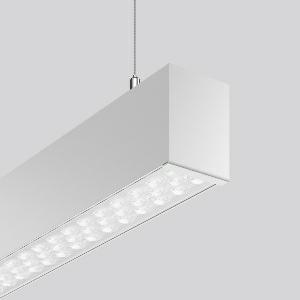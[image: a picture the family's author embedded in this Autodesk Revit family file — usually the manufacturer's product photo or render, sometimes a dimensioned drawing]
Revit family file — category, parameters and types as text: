
# Revit family: linedo_single_ip20_312563_000_1_f37b
name_source: partatom
category: Lighting Fixtures
units: mm (PartAtom-declared; Revit-internal decimal feet)

## family parameters
Cut with Voids When Loaded = No
Host = Face
Light Source = No
Part Type = Normal
Room Calculation Point = No
Round Connector Dimension = Use Diameter
Shared = No

## types (1)
- LINEDO single IP20 (1 x LED Modul 840, 4850 lm, 4000)
    Apparent Load = 31 VA
    CIE Flux Codes = 86 96 99 100 100
    Color Rendering = 80
    Color Temperature = 4000
    Default Elevation = 1800 mm
    Description = Series: LINEDO single IP20
Stylish pendant luminaire. Housing: extruded aluminium profile, anodised. End cap aluminium powder-coated, without visible screws. High-efficiency LED units with optimum light control thanks to clear plastic (PC) lens optics. 2-point steel cable suspension freely positionable and infinitely height-adjustable. With power cord (2.5 m). Please order canopy separately if required. Perfect for office areas (RUG < 19) and environments with computer screens in accordance with EN 12464-1. 
Colour: anodised aluminium
Length: 1700 mm
Width: 58 mm
Height: 76 mm
Suspension length: 100-1500 mm
Lamp: LED
Socket: without socket
Colour temperature: 4000K
Colour rendering index (CRI): 80
System power: 31 W
Rated luminous flux: 4850 lm
Beam angle Down: 59°
Luminous efficiency: 156 lm/W
Control gear: Regulated power supply
Protection class: I
Type of protection: IP 20
    Height = 76 mm
    Lamp = 1 x LED Modul 840
    Lamp Light Flux = 4850 lm
    Lamp count = 1
    Length = 1700 mm
    Lifetime = 50000 h
    Luminous efficacy = 156 lm/W
    Manufacturer = RZB
    ModVariant = No
    Model = 312563.000.1
    Mounting Place = Ceiling
    Mounting Type = Pendant
    Number of Poles = 1
    OnlyDefault = Yes
    Power Factor = 1
    Product Name = LINEDO single IP20
    Product group = Pendant luminaires
    ProductGroupID = 902
    Protection Class = Protection class I
    Protection Degree = Degree of protection
    RLX_Detail_Level = 1
    RLX_Emergency_Light_Flux = 0 lm
    RLX_Emergency_Type = 0
    RLX_Emergency_Type_DB = No
    RlxData = <blob elided: 29357 chars, md5=6e2f2f49>
    Socket = socket
    Standby Power = 0 W
    System Light Flux = 4850 lm
    System Power = 31 W
    Type Comments = ALEA SPOT
    Type Image = 312563.000.jpg
    URL = http://relux.com
    VarID = ---
    Voltage = 0 V
    Weight = 0.00 kg
    Width = 58 mm

## geometry (parser evidence)
native form markers: Blend x4, Sweep x10
no freeform markers — native parametric forms only
